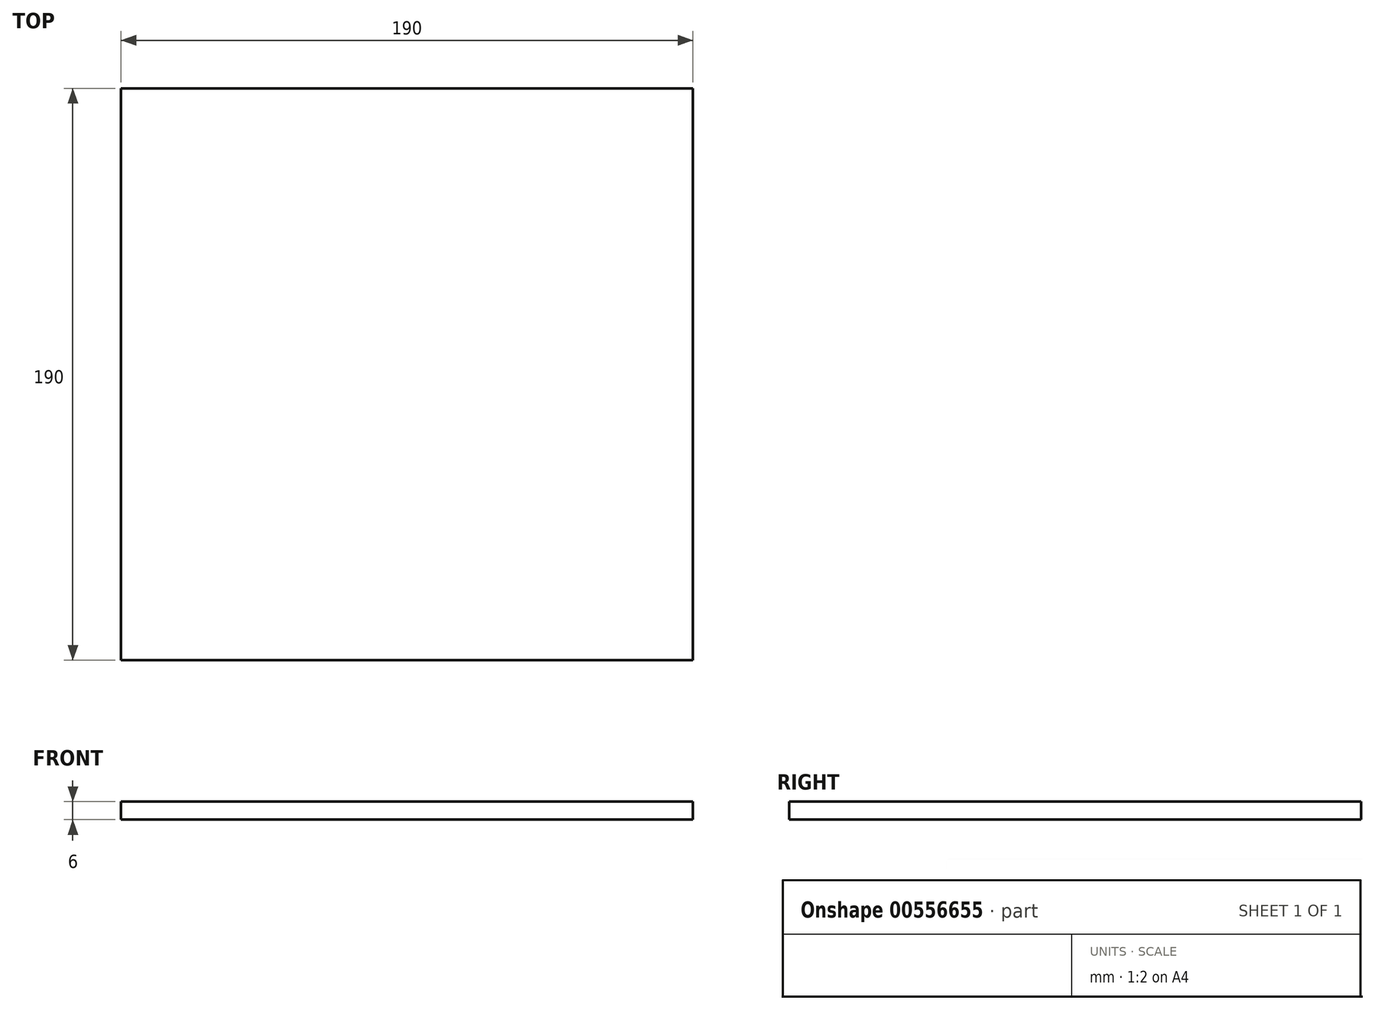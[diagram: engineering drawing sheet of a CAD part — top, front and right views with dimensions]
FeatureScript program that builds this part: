
annotation { "Feature Type Name" : "Feature", "Feature Type Description" : "" }
export const myFeature = defineFeature(function(context is Context, id is Id, definition is map)
    precondition{}
    {
        {
            var Q0;
            Q0=qCreatedBy(makeId("Top.planeOp"),FACE);
            var sketch = newSketch(context, id + "F0", { "sketchPlane" : qUnion([Q0])});
            skLineSegment(sketch, "E0", {"start": v(0, 0) * mm, "end": v(0, 190) * mm});
            skLineSegment(sketch, "E1", {"start": v(0, 190) * mm, "end": v(190, 190) * mm});
            skLineSegment(sketch, "E2", {"start": v(190, 190) * mm, "end": v(190, 0) * mm});
            skLineSegment(sketch, "E3", {"start": v(190, 0) * mm, "end": v(0, 0) * mm});
            skSolve(sketch);
        }
        {
            var Q0;
            Q0 = qSketchRegion(id + "F0", true);
            extrude(context, id + "F1", {"entities" : qUnion([Q0]), "endBound" : BoundingType.SYMMETRIC, "depth" : 6 * mm, "offsetDistance" : 25 * mm});
        }
    });
